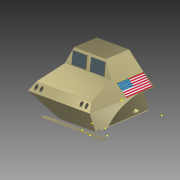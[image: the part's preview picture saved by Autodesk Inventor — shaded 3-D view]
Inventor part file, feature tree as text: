
AUTODESK INVENTOR PART (.ipt)
format: ipt  version: 2015 (Build 190159000, 159)  size: 407,040 bytes
history: native  units: in
note: dims shown in document units (in); Inventor stores cm internally (conversion verified against a paired STEP export)
features: sketch x21, extrude x9, plane x7, mirror x5, chamfer x4, other x3, fillet x1, hole x1, projected_geometry x1
ambient origin geometry x8: Origin, YZ Plane, XZ Plane, XY Plane, X Axis, Y Axis, Z Axis, Center Point
bodies: Solid1 (feature_tree)
feature tree (52):
  extrude  "Extrusion1"  Depth=3.06in
  extrude  "Extrusion2"  Depth=6.75in
  chamfer  "Chamfer1"  Distance=2.625in
  chamfer  "Chamfer2"  Distance=1.625in Angle=45.0deg
  extrude  "Extrusion3"  Depth=6.75in TaperAngle=0.0deg
  chamfer  "Chamfer3"  Distance=1.435in Angle=45.0deg
  chamfer  "Chamfer4"  Distance=1.435in Angle=45.0deg
  plane  "Work Plane1"
  extrude  "Extrusion4"  Depth=0.737in
  sketch  "Sketch5"  dims[d22=-1.38in d23=0.737in]
  plane  "Work Plane2"
  mirror  "Mirror1"
  extrude  "Extrusion5"  TaperAngle=90.0deg  [1 undecoded]
  mirror  "Mirror2"
  sketch  "Sketch7"  dims[d27=1.375in d28=1.375in d29=0.0in]
  sketch  "Sketch8"  dims[d30=1.516in d31=0.25in]
  sketch  "Sketch9"  dims[d32=0.36in d33=0.4in d34=0.0in d44=0.68in]
  other  "Work Point1"
  mirror  "Mirror3"
  plane  "Work Plane4"
  plane  "Work Plane5"
  plane  "Work Plane6"
  sketch  "Sketch10"  dims[d45=0.68in d51=0.05in d52=0.0in]
  sketch  "Sketch11"  dims[d53=2.4in d54=0.93in]
  sketch  "Sketch12"  dims[d55=0.795in]
  sketch  "Sketch13"  dims[d56=1.065in]
  extrude  "Extrusion6"  Depth=1.375in TaperAngle=0.0deg
  mirror  "Mirror4"
  sketch  "Sketch15"  dims[d59=0.2in]
  extrude  "Extrusion7"  Depth=0.25in
  extrude  "Extrusion8"  Depth=0.4in TaperAngle=0.0deg
  fillet  "Fillet1"  Radius=0.68in
  plane  "Work Plane7"
  sketch  "Sketch18"  dims[d62=1.0in]
  extrude  "Extrusion9"  Depth=0.05in TaperAngle=0.0deg
  sketch  "Sketch20"  dims[d69=1.0in]
  hole  "Hole4"  [1 undecoded]
  mirror  "Mirror6"
  sketch  "Sketch1"  dims[d0=3.17in d1=3.06in]
  sketch  "Sketch2"  dims[d2=6.75in d3=0.0in d4=0.5in]
  sketch  "Sketch3"  dims[d5=0.5in d6=2.625in d7=0.0in d8=1.625in d9=0.125in d10=45.0deg]
  sketch  "Sketch4"  dims[d11=1.625in d12=0.125in d13=45.0deg d14=6.75in d15=0.0in d16=1.435in d17=0.125in d18=45.0deg d19=1.435in d20=0.125in d21=45.0deg]
  projected_geometry  "Projected Loop1"
  plane  "Work Plane3"
  sketch  "Sketch6"  dims[d24=1.375in d25=0.0in d26=90.0deg]
  other  "Work Point2"
  sketch  "Sketch14"  dims[d57=0.57in d58=0.0in]
  other  "Image1"
  sketch  "Sketch16"  dims[d60=0.05in d61=0.0in]
  sketch  "Sketch17"  dims[d83=0.307in d84=0.75in d85=0.375in d86=0.25in d87=0.5635in d88=0.4in d89=0.8108in]
  sketch  "Sketch19"  dims[d63=1.0in]
  sketch  "Sketch24"  dims[d70=1.0in]
note: 2 required parameter values undecoded (feature->parameter linkage not recoverable at this tier; creation-order binding heuristic only, values carry confidence <= 0.55)
